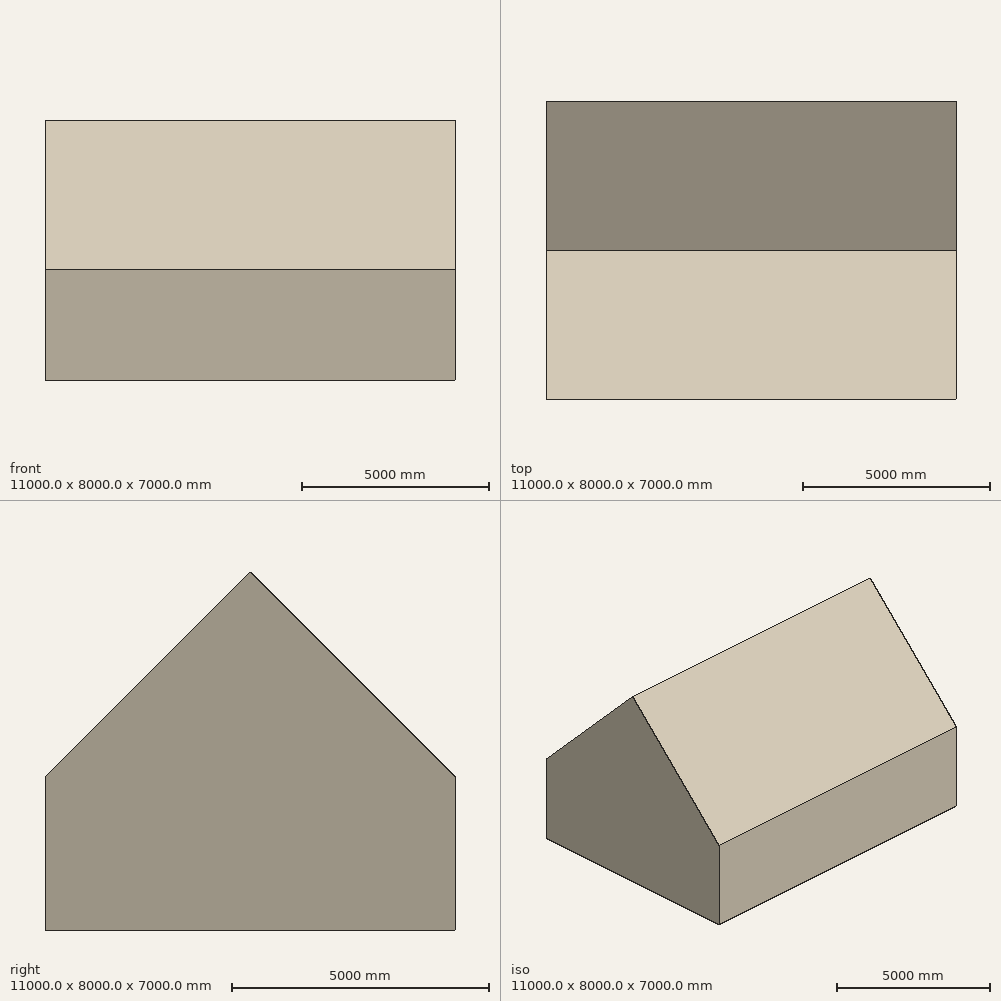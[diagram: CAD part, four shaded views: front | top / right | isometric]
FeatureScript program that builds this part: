
annotation { "Feature Type Name" : "Feature", "Feature Type Description" : "" }
export const myFeature = defineFeature(function(context is Context, id is Id, definition is map)
    precondition{}
    {
        {
            var Q0;
            Q0=qCreatedBy(makeId("Right.planeOp"),FACE);
            var sketch = newSketch(context, id + "F0", { "sketchPlane" : qUnion([Q0])});
            skLineSegment(sketch, "E0", {"start": v(-4000, 0) * mm, "end": v(-4000, 3000) * mm});
            skLineSegment(sketch, "E1", {"start": v(-4000, 3000) * mm, "end": v(0, 7000) * mm});
            skLineSegment(sketch, "E2", {"start": v(0, 7000) * mm, "end": v(4000, 3000) * mm});
            skLineSegment(sketch, "E3", {"start": v(4000, 3000) * mm, "end": v(4000, 0) * mm});
            skLineSegment(sketch, "E4", {"start": v(4000, 0) * mm, "end": v(-4000, 0) * mm});
            skSolve(sketch);
        }
        {
            var Q0;
            Q0=makeQuery(id+"F0.imprint","IMPRINT",FACE,{"disambiguationData":[TD([[makeQuery(id+"F0.imprint","IMPRINT",EDGE,{"derivedFrom":sQuery(id+"F0.wireOp",EDGE,"E0")}),-1.0]])]});
            extrude(context, id + "F1", {"entities" : qUnion([Q0]), "depth" : 11000 * mm, "offsetDistance" : 25 * mm});
        }
    });
